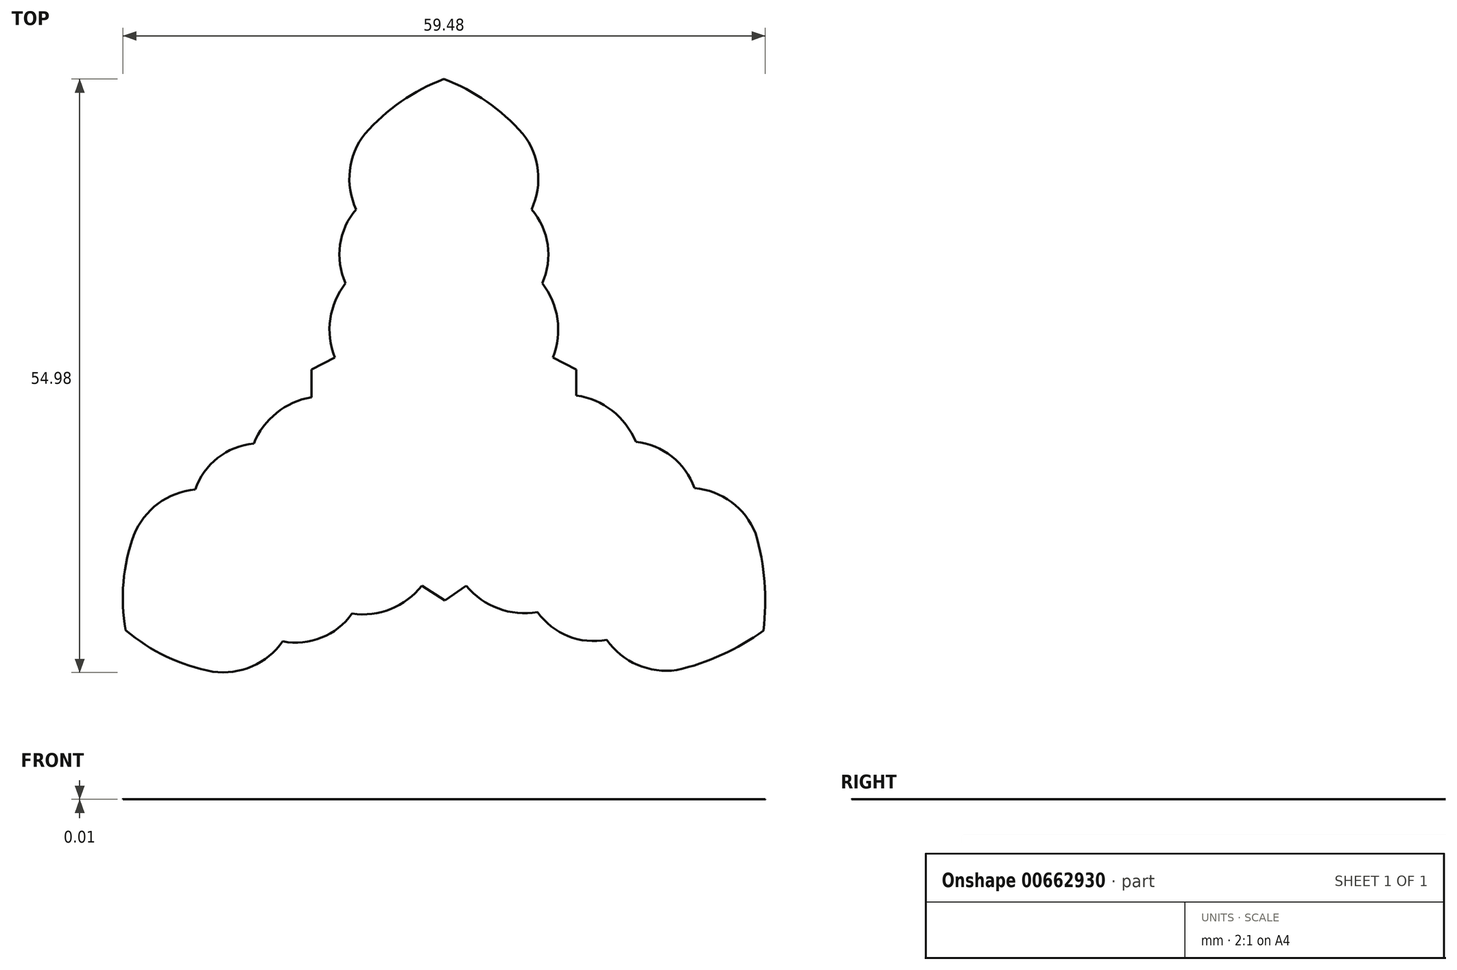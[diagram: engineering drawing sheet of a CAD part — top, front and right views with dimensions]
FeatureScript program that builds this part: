
annotation { "Feature Type Name" : "Feature", "Feature Type Description" : "" }
export const myFeature = defineFeature(function(context is Context, id is Id, definition is map)
    precondition{}
    {
        {
            var Q0;
            Q0=qCreatedBy(makeId("Top.planeOp"),FACE);
            var sketch = newSketch(context, id + "F0", { "sketchPlane" : qUnion([Q0])});
            skPoint(sketch, "E0.center", {"position": v(0, 0) * mm});
            skArc(sketch, "E1", {"start": v(-7.42, 28.98) * mm, "mid": v(-8.81, 25.6) * mm, "end": v(-8.23, 21.98) * mm});
            skArc(sketch, "E2", {"start": v(-8.23, 21.98) * mm, "mid": v(-9.72, 18.7) * mm, "end": v(-9.2, 15.13) * mm});
            skArc(sketch, "E3", {"start": v(-9.2, 15.13) * mm, "mid": v(-10.62, 11.82) * mm, "end": v(-10.2, 8.25) * mm});
            skLineSegment(sketch, "E4", {"start": v(-10.2, 8.25) * mm, "end": v(-12.37, 7.15) * mm});
            skLineSegment(sketch, "E5", {"start": v(-12.37, 7.15) * mm, "end": v(-12.37, 4.64) * mm});
            skLineSegment(sketch, "E6.MirrorCS", {"start": v(12.16, 7.15) * mm, "end": v(12.16, 4.64) * mm});
            skLineSegment(sketch, "E7.MirrorCS", {"start": v(10, 8.25) * mm, "end": v(12.16, 7.15) * mm});
            skArc(sketch, "E8.MirrorCS", {"start": v(9, 15.13) * mm, "mid": v(10.4, 11.82) * mm, "end": v(10, 8.25) * mm});
            skArc(sketch, "E9.MirrorCS", {"start": v(8.01, 21.98) * mm, "mid": v(9.5, 18.7) * mm, "end": v(9, 15.13) * mm});
            skArc(sketch, "E10.MirrorCS", {"start": v(7.2, 28.98) * mm, "mid": v(8.6, 25.6) * mm, "end": v(8.01, 21.98) * mm});
            skArc(sketch, "E11", {"start": v(28.76, -8.05) * mm, "mid": v(26.53, -5.15) * mm, "end": v(23.1, -3.85) * mm});
            skArc(sketch, "E12", {"start": v(23.1, -3.85) * mm, "mid": v(21, -0.92) * mm, "end": v(17.66, 0.43) * mm});
            skArc(sketch, "E13", {"start": v(17.66, 0.43) * mm, "mid": v(15.48, 3.32) * mm, "end": v(12.16, 4.74) * mm});
            skArc(sketch, "E14.MirrorCS", {"start": v(8.56, -15.34) * mm, "mid": v(4.94, -15) * mm, "end": v(1.97, -12.9) * mm});
            skArc(sketch, "E15.MirrorCS", {"start": v(14.98, -17.91) * mm, "mid": v(11.4, -17.56) * mm, "end": v(8.56, -15.34) * mm});
            skArc(sketch, "E16.MirrorCS", {"start": v(21.45, -20.71) * mm, "mid": v(17.82, -20.23) * mm, "end": v(14.98, -17.91) * mm});
            skLineSegment(sketch, "E17", {"start": v(1.97, -12.9) * mm, "end": v(0, -14.26) * mm});
            skLineSegment(sketch, "E18", {"start": v(0, -14.26) * mm, "end": v(-2.14, -12.9) * mm});
            skArc(sketch, "E19", {"start": v(-21.5, -20.86) * mm, "mid": v(-17.86, -20.37) * mm, "end": v(-15.02, -18.05) * mm});
            skArc(sketch, "E20", {"start": v(-15.02, -18.05) * mm, "mid": v(-11.43, -17.7) * mm, "end": v(-8.6, -15.48) * mm});
            skArc(sketch, "E21", {"start": v(-8.6, -15.48) * mm, "mid": v(-5.03, -15.05) * mm, "end": v(-2.14, -12.9) * mm});
            skArc(sketch, "E22.MirrorCS", {"start": v(-17.7, 0.28) * mm, "mid": v(-15.6, 3.12) * mm, "end": v(-12.37, 4.57) * mm});
            skArc(sketch, "E23.MirrorCS", {"start": v(-23.14, -4) * mm, "mid": v(-21.05, -1.06) * mm, "end": v(-17.7, 0.28) * mm});
            skArc(sketch, "E24.MirrorCS", {"start": v(-28.8, -8.2) * mm, "mid": v(-26.56, -5.3) * mm, "end": v(-23.14, -4) * mm});
            skLineSegment(sketch, "E25", {"start": v(-12.37, 4.64) * mm, "end": v(-12.37, 4.57) * mm});
            skArc(sketch, "E26", {"start": v(-0.1, 34.05) * mm, "mid": v(-4.07, 31.97) * mm, "end": v(-7.42, 28.98) * mm});
            skArc(sketch, "E27", {"start": v(7.2, 28.98) * mm, "mid": v(3.87, 31.97) * mm, "end": v(-0.1, 34.05) * mm});
            skArc(sketch, "E28", {"start": v(21.45, -20.71) * mm, "mid": v(25.66, -19.3) * mm, "end": v(29.48, -17.04) * mm});
            skArc(sketch, "E29", {"start": v(29.48, -17.04) * mm, "mid": v(29.58, -12.51) * mm, "end": v(28.76, -8.05) * mm});
            skArc(sketch, "E30", {"start": v(-28.8, -8.2) * mm, "mid": v(-29.77, -12.56) * mm, "end": v(-29.56, -17.02) * mm});
            skArc(sketch, "E31", {"start": v(-29.56, -17.02) * mm, "mid": v(-25.78, -19.47) * mm, "end": v(-21.5, -20.86) * mm});
            skSolve(sketch);
        }
        {
            var Q0;
            Q0=makeQuery(id+"F0.imprint","IMPRINT",FACE,{"disambiguationData":[TD([[makeQuery(id+"F0.imprint","IMPRINT",EDGE,{"derivedFrom":sQuery(id+"F0.wireOp",EDGE,"E1")}),1.0]])]});
            extrude(context, id + "F1", {"entities" : qUnion([Q0]), "depth" : 5 / 406.4 * mm, "offsetDistance" : 25.4 * mm});
        }
    });
